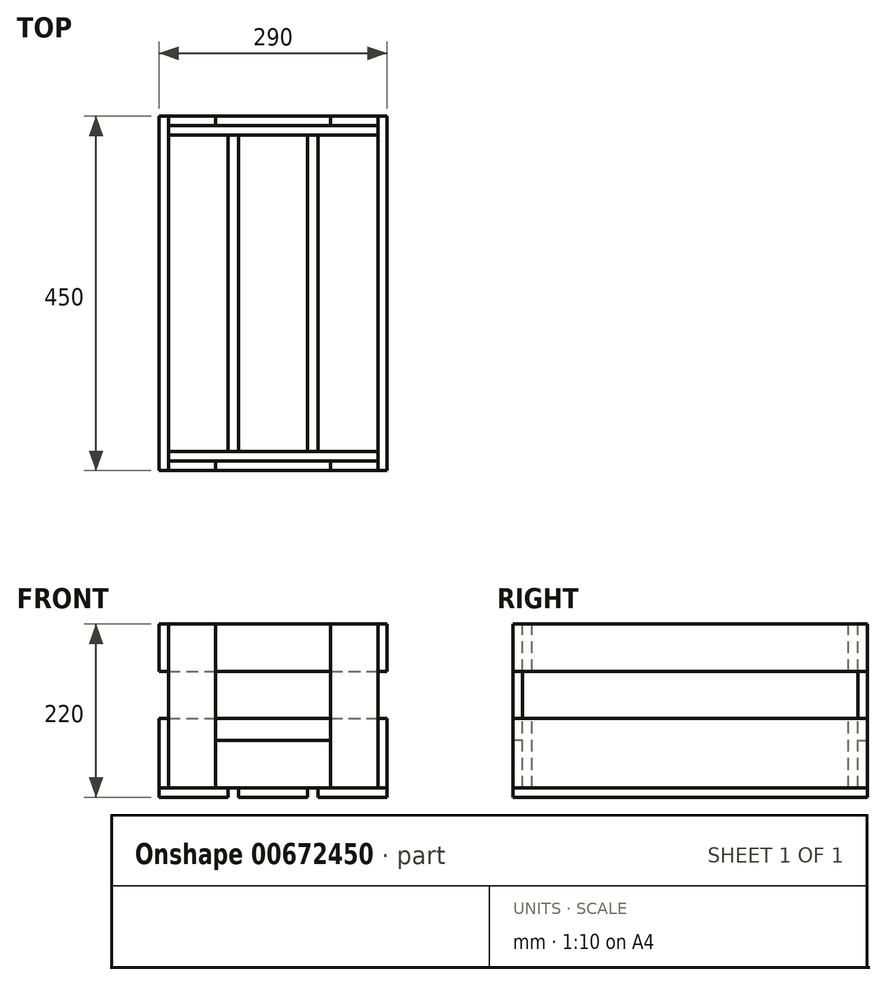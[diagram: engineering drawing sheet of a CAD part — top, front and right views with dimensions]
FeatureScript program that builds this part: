
annotation { "Feature Type Name" : "Feature", "Feature Type Description" : "" }
export const myFeature = defineFeature(function(context is Context, id is Id, definition is map)
    precondition{}
    {
        {
            var Q0;
            Q0=qCreatedBy(makeId("Top.planeOp"),FACE);
            var sketch = newSketch(context, id + "F0", { "sketchPlane" : qUnion([Q0])});
            skLineSegment(sketch, "E0.bottom", {"start": v(0, 0) * mm, "end": v(290, 0) * mm});
            skLineSegment(sketch, "E0.top", {"start": v(0, 450) * mm, "end": v(290, 450) * mm});
            skLineSegment(sketch, "E0.left", {"start": v(0, 0) * mm, "end": v(0, 450) * mm});
            skLineSegment(sketch, "E0.right", {"start": v(290, 0) * mm, "end": v(290, 450) * mm});
            skLineSegment(sketch, "E1", {"start": v(290, 225) * mm, "end": v(0, 225) * mm});
            skSolve(sketch);
        }
        {
            var Q0;
            Q0 = qSketchRegion(id + "F0", true);
            extrude(context, id + "F1", {"entities" : qUnion([Q0]), "depth" : 220 * mm, "offsetDistance" : 25 * mm});
        }
        {
            var Q0;
            Q0=makeQuery(id+"F1.opExtrude","SWEPT_FACE",FACE,{"disambiguationData":[OSD([sQuery(id+"F0.wireOp",EDGE,"E0.top")])]});
            var sketch = newSketch(context, id + "F2", { "sketchPlane" : qUnion([Q0])});
            skLineSegment(sketch, "E2.bottom", {"start": v(0, 0) * mm, "end": v(-290, 0) * mm});
            skLineSegment(sketch, "E2.top", {"start": v(0, 220) * mm, "end": v(-290, 220) * mm});
            skLineSegment(sketch, "E2.left", {"start": v(0, 0) * mm, "end": v(0, 220) * mm});
            skLineSegment(sketch, "E2.right", {"start": v(-290, 0) * mm, "end": v(-290, 220) * mm});
            skLineSegment(sketch, "E3.0", {"start": v(0, 12) * mm, "end": v(-290, 12) * mm});
            skLineSegment(sketch, "E4.0", {"start": v(-278, 0) * mm, "end": v(-278, 220) * mm});
            skLineSegment(sketch, "E5.0", {"start": v(-12, 0) * mm, "end": v(-12, 220) * mm});
            skLineSegment(sketch, "E6.0", {"start": v(-202, 0) * mm, "end": v(-202, 12) * mm});
            skLineSegment(sketch, "E7.0", {"start": v(-88, 0) * mm, "end": v(-88, 12) * mm});
            skLineSegment(sketch, "E8.0", {"start": v(-101, 0) * mm, "end": v(-101, 12) * mm});
            skLineSegment(sketch, "E9.0", {"start": v(-189, 0) * mm, "end": v(-189, 12) * mm});
            skLineSegment(sketch, "E10.0", {"start": v(0, 100) * mm, "end": v(-12, 100) * mm});
            skLineSegment(sketch, "E11.0", {"start": v(0, 160) * mm, "end": v(-12, 160) * mm});
            skLineSegment(sketch, "E12.trimOffspring", {"start": v(-278, 160) * mm, "end": v(-290, 160) * mm});
            skLineSegment(sketch, "E13.trimOffspring", {"start": v(-278, 100) * mm, "end": v(-290, 100) * mm});
            skLineSegment(sketch, "E14.0", {"start": v(-72, 12) * mm, "end": v(-72, 72) * mm});
            skLineSegment(sketch, "E15.0", {"start": v(-218, 12) * mm, "end": v(-218, 72) * mm});
            skLineSegment(sketch, "E16.0", {"start": v(-72, 72) * mm, "end": v(-218, 72) * mm});
            skSolve(sketch);
        }
        {
            var Q0;
            {var subQ5=sQuery(id+"F2.wireOp",EDGE,"E12.trimOffspring");Q0=makeQuery(id+"F2.imprint","IMPRINT",FACE,{"disambiguationData":[TD([[makeQuery(id+"F2.imprint","IMPRINT",EDGE,{"derivedFrom":subQ5}),-1.0]])]});}
            var Q1;
            {var subQ3=sQuery(id+"F2.wireOp",EDGE,"E6.0");Q1=makeQuery(id+"F2.imprint","IMPRINT",FACE,{"disambiguationData":[TD([[makeQuery(id+"F2.imprint","IMPRINT",EDGE,{"derivedFrom":subQ3}),1.0]])]});}
            var Q2;
            {var subQ0=sQuery(id+"F2.wireOp",EDGE,"E2.right");var subQ1=sQuery(id+"F2.wireOp",EDGE,"E2.bottom");var subQ2=makeQuery(id+"F2.imprint","INTERSECT",VERTEX,{"derivedFrom":[subQ1,subQ0]});Q2=makeQuery(id+"F2.imprint","IMPRINT",FACE,{"disambiguationData":[TD([[makeQuery(id+"F2.imprint","IMPRINT",EDGE,{"disambiguationData":[TD([[subQ2,1.0]])],"derivedFrom":subQ1}),-1.0]])]});}
            var Q3;
            {var subQ0=sQuery(id+"F2.wireOp",EDGE,"E8.0");Q3=makeQuery(id+"F2.imprint","IMPRINT",FACE,{"disambiguationData":[TD([[makeQuery(id+"F2.imprint","IMPRINT",EDGE,{"derivedFrom":subQ0}),1.0]])]});}
            var Q4;
            {var subQ3=sQuery(id+"F2.wireOp",EDGE,"E7.0");Q4=makeQuery(id+"F2.imprint","IMPRINT",FACE,{"disambiguationData":[TD([[makeQuery(id+"F2.imprint","IMPRINT",EDGE,{"derivedFrom":subQ3}),-1.0]])]});}
            var Q5;
            {var subQ0=sQuery(id+"F2.wireOp",EDGE,"E2.left");var subQ1=sQuery(id+"F2.wireOp",EDGE,"E2.bottom");var subQ2=makeQuery(id+"F2.imprint","INTERSECT",VERTEX,{"derivedFrom":[subQ1,subQ0]});Q5=makeQuery(id+"F2.imprint","IMPRINT",FACE,{"disambiguationData":[TD([[makeQuery(id+"F2.imprint","IMPRINT",EDGE,{"disambiguationData":[TD([[subQ2,-1.0]])],"derivedFrom":subQ1}),-1.0]])]});}
            var Q6;
            {var subQ5=sQuery(id+"F2.wireOp",EDGE,"E11.0");Q6=makeQuery(id+"F2.imprint","IMPRINT",FACE,{"disambiguationData":[TD([[makeQuery(id+"F2.imprint","IMPRINT",EDGE,{"derivedFrom":subQ5}),-1.0]])]});}
            var Q7;
            Q7=makeQuery(id+"F1.opExtrude","CAP_VERTEX",VERTEX,{"disambiguationData":[OSD([sQuery(id+"F0.wireOp",EDGE,"E0.bottom"),sQuery(id+"F0.wireOp",EDGE,"E0.left")])],"isStart":false});
            extrude(context, id + "F3", {"entities" : qUnion([Q0, Q1, Q2, Q3, Q4, Q5, Q6]), "endBound" : BoundingType.UP_TO_VERTEX, "oppositeDirection" : true, "depth" : 25 * mm, "endBoundEntityVertex" : qUnion([Q7]), "offsetDistance" : 25 * mm});
        }
        {
            var Q0;
            {var subQ3=sQuery(id+"F2.wireOp",EDGE,"E13.trimOffspring");Q0=makeQuery(id+"F2.imprint","IMPRINT",FACE,{"disambiguationData":[TD([[makeQuery(id+"F2.imprint","IMPRINT",EDGE,{"derivedFrom":subQ3}),1.0]])]});}
            var Q1;
            {var subQ3=sQuery(id+"F2.wireOp",EDGE,"E10.0");Q1=makeQuery(id+"F2.imprint","IMPRINT",FACE,{"disambiguationData":[TD([[makeQuery(id+"F2.imprint","IMPRINT",EDGE,{"derivedFrom":subQ3}),1.0]])]});}
            var Q2;
            Q2=makeQuery(id+"F3.opExtrude","CAP_VERTEX",VERTEX,{"disambiguationData":[OSD([sQuery(id+"F2.wireOp",EDGE,"E2.left"),sQuery(id+"F2.wireOp",EDGE,"E3.0"),dummyQuery(id+"F3.vertexPlane.planeOp",FACE)])],"isStart":false});
            extrude(context, id + "F4", {"entities" : qUnion([Q0, Q1]), "endBound" : BoundingType.UP_TO_VERTEX, "oppositeDirection" : true, "depth" : 25 * mm, "endBoundEntityVertex" : qUnion([Q2]), "offsetDistance" : 25 * mm});
        }
        {
            var Q0;
            Q0=makeQuery(id+"F1.opExtrude","CAP_FACE",FACE,{"disambiguationData":[OSD([sQuery(id+"F0.wireOp",EDGE,"E0.bottom"),sQuery(id+"F0.wireOp",EDGE,"E0.top"),sQuery(id+"F0.wireOp",EDGE,"E0.left"),sQuery(id+"F0.wireOp",EDGE,"E0.right")])],"isStart":false});
            var sketch = newSketch(context, id + "F5", { "sketchPlane" : qUnion([Q0])});
            skLineSegment(sketch, "E17", {"start": v(0, 0) * mm, "end": v(290, 0) * mm});
            skLineSegment(sketch, "E18.0", {"start": v(0, 12) * mm, "end": v(290, 12) * mm});
            skLineSegment(sketch, "E19.0", {"start": v(0, 24) * mm, "end": v(290, 24) * mm});
            skLineSegment(sketch, "E20", {"start": v(0, 0) * mm, "end": v(0, 24) * mm});
            skLineSegment(sketch, "E21.0", {"start": v(12, 0) * mm, "end": v(12, 24) * mm});
            skLineSegment(sketch, "E22.0", {"start": v(72, 0) * mm, "end": v(72, 24) * mm});
            skLineSegment(sketch, "E23", {"start": v(145, 0) * mm, "end": v(145, 24) * mm});
            skLineSegment(sketch, "E24.MirrorCS", {"start": v(218, 0) * mm, "end": v(218, 24) * mm});
            skLineSegment(sketch, "E25.MirrorCS", {"start": v(278, 0) * mm, "end": v(278, 24) * mm});
            skSolve(sketch);
        }
        {
            var Q0;
            {var subQ0=sQuery(id+"F5.wireOp",EDGE,"E21.0");var subQ1=sQuery(id+"F5.wireOp",EDGE,"E17");var subQ2=makeQuery(id+"F5.imprint","INTERSECT",VERTEX,{"derivedFrom":[subQ1,subQ0]});Q0=makeQuery(id+"F5.imprint","IMPRINT",FACE,{"disambiguationData":[TD([[makeQuery(id+"F5.imprint","IMPRINT",EDGE,{"disambiguationData":[TD([[subQ2,-1.0]])],"derivedFrom":subQ1}),1.0]])]});}
            var Q1;
            {var subQ0=sQuery(id+"F5.wireOp",EDGE,"E24.MirrorCS");var subQ1=sQuery(id+"F5.wireOp",EDGE,"E17");var subQ2=makeQuery(id+"F5.imprint","INTERSECT",VERTEX,{"derivedFrom":[subQ1,subQ0]});Q1=makeQuery(id+"F5.imprint","IMPRINT",FACE,{"disambiguationData":[TD([[makeQuery(id+"F5.imprint","IMPRINT",EDGE,{"disambiguationData":[TD([[subQ2,-1.0]])],"derivedFrom":subQ1}),1.0]])]});}
            var Q2;
            Q2=makeQuery(id+"F4.opExtrude","CAP_VERTEX",VERTEX,{"disambiguationData":[OSD([sQuery(id+"F2.wireOp",EDGE,"E3.0"),sQuery(id+"F2.wireOp",EDGE,"E5.0"),dummyQuery(id+"F4.vertexPlane.planeOp",FACE)])],"isStart":false});
            extrude(context, id + "F6", {"entities" : qUnion([Q0, Q1]), "endBound" : BoundingType.UP_TO_VERTEX, "oppositeDirection" : true, "depth" : 25 * mm, "endBoundEntityVertex" : qUnion([Q2]), "offsetDistance" : 25 * mm});
        }
        {
            var Q0;
            {var subQ0=sQuery(id+"F5.wireOp",EDGE,"E21.0");var subQ1=sQuery(id+"F5.wireOp",EDGE,"E18.0");var subQ2=makeQuery(id+"F5.imprint","INTERSECT",VERTEX,{"derivedFrom":[subQ1,subQ0]});Q0=makeQuery(id+"F5.imprint","IMPRINT",FACE,{"disambiguationData":[TD([[makeQuery(id+"F5.imprint","IMPRINT",EDGE,{"disambiguationData":[TD([[subQ2,-1.0]])],"derivedFrom":subQ1}),1.0]])]});}
            var Q1;
            {var subQ0=sQuery(id+"F5.wireOp",EDGE,"E22.0");var subQ1=sQuery(id+"F5.wireOp",EDGE,"E18.0");var subQ2=makeQuery(id+"F5.imprint","INTERSECT",VERTEX,{"derivedFrom":[subQ1,subQ0]});Q1=makeQuery(id+"F5.imprint","IMPRINT",FACE,{"disambiguationData":[TD([[makeQuery(id+"F5.imprint","IMPRINT",EDGE,{"disambiguationData":[TD([[subQ2,-1.0]])],"derivedFrom":subQ1}),1.0]])]});}
            var Q2;
            {var subQ0=sQuery(id+"F5.wireOp",EDGE,"E23");var subQ1=sQuery(id+"F5.wireOp",EDGE,"E18.0");var subQ2=makeQuery(id+"F5.imprint","INTERSECT",VERTEX,{"derivedFrom":[subQ1,subQ0]});Q2=makeQuery(id+"F5.imprint","IMPRINT",FACE,{"disambiguationData":[TD([[makeQuery(id+"F5.imprint","IMPRINT",EDGE,{"disambiguationData":[TD([[subQ2,-1.0]])],"derivedFrom":subQ1}),1.0]])]});}
            var Q3;
            {var subQ0=sQuery(id+"F5.wireOp",EDGE,"E24.MirrorCS");var subQ1=sQuery(id+"F5.wireOp",EDGE,"E18.0");var subQ2=makeQuery(id+"F5.imprint","INTERSECT",VERTEX,{"derivedFrom":[subQ1,subQ0]});Q3=makeQuery(id+"F5.imprint","IMPRINT",FACE,{"disambiguationData":[TD([[makeQuery(id+"F5.imprint","IMPRINT",EDGE,{"disambiguationData":[TD([[subQ2,-1.0]])],"derivedFrom":subQ1}),1.0]])]});}
            extrude(context, id + "F7", {"entities" : qUnion([Q0, Q1, Q2, Q3]), "oppositeDirection" : true, "depth" : 60 * mm, "offsetDistance" : 25 * mm});
        }
        {
            var Q0;
            {var subQ0=sQuery(id+"F5.wireOp",EDGE,"E21.0");var subQ1=sQuery(id+"F5.wireOp",EDGE,"E18.0");var subQ2=makeQuery(id+"F5.imprint","INTERSECT",VERTEX,{"derivedFrom":[subQ1,subQ0]});Q0=makeQuery(id+"F5.imprint","IMPRINT",FACE,{"disambiguationData":[TD([[makeQuery(id+"F5.imprint","IMPRINT",EDGE,{"disambiguationData":[TD([[subQ2,-1.0]])],"derivedFrom":subQ1}),1.0]])]});}
            var Q1;
            {var subQ0=sQuery(id+"F5.wireOp",EDGE,"E22.0");var subQ1=sQuery(id+"F5.wireOp",EDGE,"E18.0");var subQ2=makeQuery(id+"F5.imprint","INTERSECT",VERTEX,{"derivedFrom":[subQ1,subQ0]});Q1=makeQuery(id+"F5.imprint","IMPRINT",FACE,{"disambiguationData":[TD([[makeQuery(id+"F5.imprint","IMPRINT",EDGE,{"disambiguationData":[TD([[subQ2,-1.0]])],"derivedFrom":subQ1}),1.0]])]});}
            var Q2;
            {var subQ0=sQuery(id+"F5.wireOp",EDGE,"E23");var subQ1=sQuery(id+"F5.wireOp",EDGE,"E18.0");var subQ2=makeQuery(id+"F5.imprint","INTERSECT",VERTEX,{"derivedFrom":[subQ1,subQ0]});Q2=makeQuery(id+"F5.imprint","IMPRINT",FACE,{"disambiguationData":[TD([[makeQuery(id+"F5.imprint","IMPRINT",EDGE,{"disambiguationData":[TD([[subQ2,-1.0]])],"derivedFrom":subQ1}),1.0]])]});}
            var Q3;
            {var subQ0=sQuery(id+"F5.wireOp",EDGE,"E24.MirrorCS");var subQ1=sQuery(id+"F5.wireOp",EDGE,"E18.0");var subQ2=makeQuery(id+"F5.imprint","INTERSECT",VERTEX,{"derivedFrom":[subQ1,subQ0]});Q3=makeQuery(id+"F5.imprint","IMPRINT",FACE,{"disambiguationData":[TD([[makeQuery(id+"F5.imprint","IMPRINT",EDGE,{"disambiguationData":[TD([[subQ2,-1.0]])],"derivedFrom":subQ1}),1.0]])]});}
            var Q4;
            Q4=makeQuery(id+"F6.opExtrude","CAP_VERTEX",VERTEX,{"disambiguationData":[OSD([sQuery(id+"F5.wireOp",EDGE,"E17"),sQuery(id+"F5.wireOp",EDGE,"E21.0"),dummyQuery(id+"F6.vertexPlane.planeOp",FACE)])],"isStart":false});
            var Q5;
            Q5=makeQuery(id+"F4.opExtrude","CAP_VERTEX",VERTEX,{"disambiguationData":[OSD([sQuery(id+"F2.wireOp",EDGE,"E5.0"),sQuery(id+"F2.wireOp",EDGE,"E10.0"),dummyQuery(id+"F4.vertexPlane.planeOp",FACE)])],"isStart":false});
            extrude(context, id + "F8", {"entities" : qUnion([Q0, Q1, Q2, Q3]), "endBound" : BoundingType.UP_TO_VERTEX, "oppositeDirection" : true, "depth" : 25 * mm, "endBoundEntityVertex" : qUnion([Q4]), "offsetDistance" : 25 * mm, "hasSecondDirection" : true, "secondDirectionBound" : BoundingType.UP_TO_VERTEX, "secondDirectionOppositeDirection" : true, "secondDirectionDepth" : 25 * mm, "secondDirectionBoundEntityVertex" : qUnion([Q5])});
        }
        {
            var Q0;
            {var subQ6=sQuery(id+"F2.wireOp",EDGE,"E14.0");Q0=makeQuery(id+"F2.imprint","IMPRINT",FACE,{"disambiguationData":[TD([[makeQuery(id+"F2.imprint","IMPRINT",EDGE,{"derivedFrom":subQ6}),1.0]])]});}
            extrude(context, id + "F9", {"entities" : qUnion([Q0]), "oppositeDirection" : true, "depth" : 12 * mm, "offsetDistance" : 25 * mm});
        }
        {
            var Q0;
            {var subQ0=sQuery(id+"F0.wireOp",EDGE,"E0.bottom");Q0=makeQuery(id+"F0.imprint","IMPRINT",FACE,{"disambiguationData":[TD([[makeQuery(id+"F0.imprint","IMPRINT",EDGE,{"derivedFrom":subQ0}),1.0]])]});}
            extrude(context, id + "F10", {"entities" : qUnion([Q0]), "depth" : 25 * mm, "offsetDistance" : 25 * mm});
        }
        {
            var Q0;
            Q0=makeQuery(id+"F9.opExtrude","SWEPT_BODY",BODY,{"disambiguationData":[OSD([sQuery(id+"F2.wireOp",EDGE,"E3.0"),sQuery(id+"F2.wireOp",EDGE,"E14.0"),sQuery(id+"F2.wireOp",EDGE,"E15.0"),sQuery(id+"F2.wireOp",EDGE,"E16.0")])]});
            var Q1;
            Q1=makeQuery(id+"F6.opExtrude","SWEPT_BODY",BODY,{"disambiguationData":[OSD([sQuery(id+"F5.wireOp",EDGE,"E17"),sQuery(id+"F5.wireOp",EDGE,"E18.0"),sQuery(id+"F5.wireOp",EDGE,"E24.MirrorCS"),sQuery(id+"F5.wireOp",EDGE,"E25.MirrorCS")])]});
            var Q2;
            Q2=makeQuery(id+"F7.opExtrude","SWEPT_BODY",BODY,{"disambiguationData":[OSD([sQuery(id+"F5.wireOp",EDGE,"E18.0"),sQuery(id+"F5.wireOp",EDGE,"E19.0"),sQuery(id+"F5.wireOp",EDGE,"E21.0"),sQuery(id+"F5.wireOp",EDGE,"E25.MirrorCS")])]});
            var Q3;
            Q3=makeQuery(id+"F8.opExtrude","SWEPT_BODY",BODY,{"disambiguationData":[OSD([sQuery(id+"F5.wireOp",EDGE,"E18.0"),sQuery(id+"F5.wireOp",EDGE,"E19.0"),sQuery(id+"F5.wireOp",EDGE,"E21.0"),sQuery(id+"F5.wireOp",EDGE,"E25.MirrorCS")])]});
            var Q4;
            Q4=makeQuery(id+"F6.opExtrude","SWEPT_BODY",BODY,{"disambiguationData":[OSD([sQuery(id+"F5.wireOp",EDGE,"E17"),sQuery(id+"F5.wireOp",EDGE,"E18.0"),sQuery(id+"F5.wireOp",EDGE,"E21.0"),sQuery(id+"F5.wireOp",EDGE,"E22.0")])]});
            var Q5;
            Q5=makeQuery(id+"F10.opExtrude","SWEPT_FACE",FACE,{"disambiguationData":[OSD([sQuery(id+"F0.wireOp",EDGE,"E1")])]});
            mirror(context, id + "F11", {"entities" : qUnion([Q0, Q1, Q2, Q3, Q4]), "mirrorPlane" : qUnion([Q5])});
        }
        {
            var Q0;
            Q0=makeQuery(id+"F10.opExtrude","SWEPT_BODY",BODY,{"disambiguationData":[OSD([sQuery(id+"F0.wireOp",EDGE,"E0.bottom"),sQuery(id+"F0.wireOp",EDGE,"E0.left"),sQuery(id+"F0.wireOp",EDGE,"E0.right"),sQuery(id+"F0.wireOp",EDGE,"E1")])]});
            deleteBodies(context, id + "F12", {"entities" : qUnion([Q0])});
        }
        {
            var Q0;
            Q0=makeQuery(id+"F1.opExtrude","SWEPT_BODY",BODY,{"disambiguationData":[OSD([sQuery(id+"F0.wireOp",EDGE,"E0.bottom"),sQuery(id+"F0.wireOp",EDGE,"E0.top"),sQuery(id+"F0.wireOp",EDGE,"E0.left"),sQuery(id+"F0.wireOp",EDGE,"E0.right")])]});
            deleteBodies(context, id + "F13", {"entities" : qUnion([Q0])});
        }
    });
